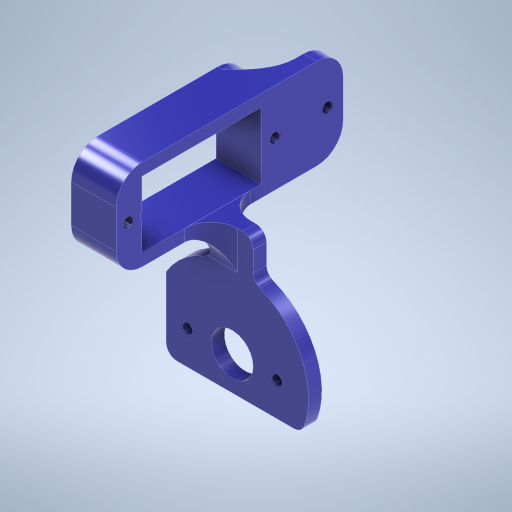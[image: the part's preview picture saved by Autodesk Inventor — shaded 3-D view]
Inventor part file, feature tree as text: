
AUTODESK INVENTOR PART (.ipt)
format: ipt  version: 2023.2 (Build 272271000, 271)  size: 414,208 bytes
history: native  units: mm
features: extrude x4, fillet x4, sketch x4
ambient origin geometry x8: Origin, YZ Plane, XZ Plane, XY Plane, X Axis, Y Axis, Z Axis, Center Point
bodies: Solid1 (feature_tree)
feature tree (12):
  extrude  "Extrusion1"  Depth=2.5mm TaperAngle=0.0deg
  extrude  "Extrusion2"  Depth=2.0mm
  fillet  "Fillet1"  Radius=2.0mm
  extrude  "Extrusion4"  Depth=2.5mm
  fillet  "Fillet2"  Radius=8.0mm
  fillet  "Fillet3"  Radius=2.5mm
  extrude  "Extrusion5"  Depth=2.0mm
  fillet  "Fillet4"  Radius=27.8mm
  sketch  "Sketch1"  dims[d0=12.6mm d2=2.5mm d3=0.0mm]
  sketch  "Sketch2"  dims[d4=29.0mm d5=17.0mm d6=2.0mm]
  sketch  "Sketch4"  dims[d7=2.0mm d8=8.0mm d9=8.0mm d10=2.5mm d11=0.0mm]
  sketch  "Sketch5"  dims[d12=5.0mm d13=2.0mm d14=27.8mm d15=8.7mm d16=2.0mm d17=2.0mm d18=12.6mm d19=11.4mm d20=5.0mm d21=12.6mm d22=22.6mm d23=2.6mm d26=6.0mm d27=0.0mm d28=2.0mm d29=4.9mm d30=3.0mm d31=5.0mm d32=17.658042mm d33=5.020146mm d34=42.428mm d35=5.0mm d36=2.5mm d37=0.0mm d38=2.0mm d24=0.5mm d25=0.872665mm]
